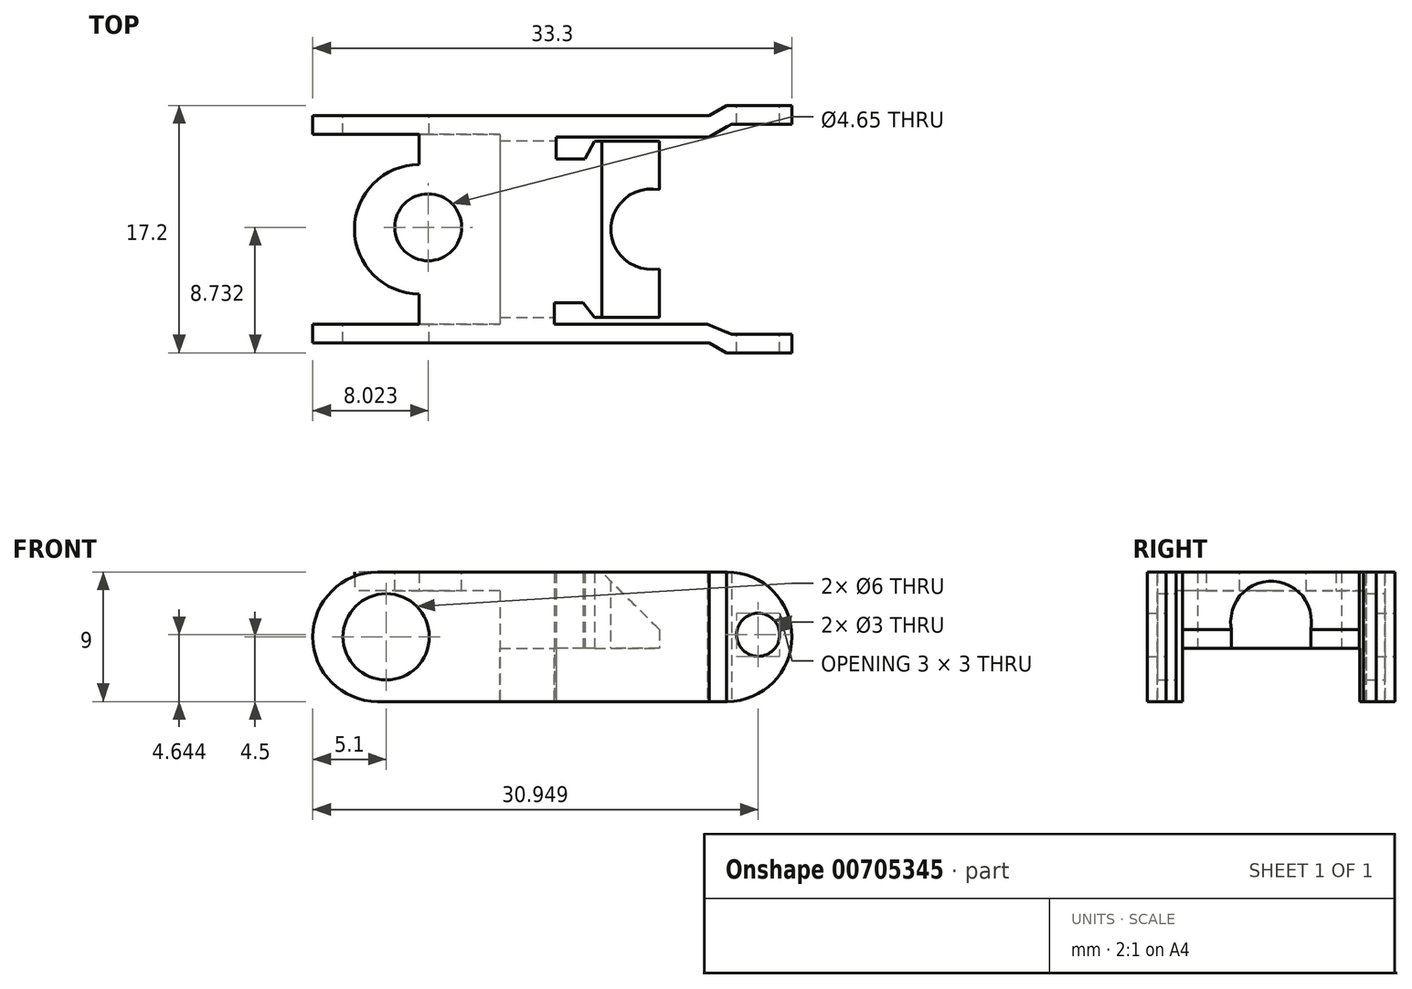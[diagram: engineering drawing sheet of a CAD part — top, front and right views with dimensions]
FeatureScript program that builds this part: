
annotation { "Feature Type Name" : "Feature", "Feature Type Description" : "" }
export const myFeature = defineFeature(function(context is Context, id is Id, definition is map)
    precondition{}
    {
        {
            var Q0;
            Q0=qCreatedBy(makeId("Top.planeOp"),FACE);
            var sketch = newSketch(context, id + "F0", { "sketchPlane" : qUnion([Q0])});
            skLineSegment(sketch, "E0", {"start": v(0, 0) * mm, "end": v(0, 1.3) * mm});
            skLineSegment(sketch, "E1", {"start": v(0, 1.3) * mm, "end": v(7.4, 1.3) * mm});
            skLineSegment(sketch, "E2", {"start": v(7.4, 1.3) * mm, "end": v(7.4, 3.4) * mm});
            skArc(sketch, "E3", {"start": v(7.4, 12.4) * mm, "mid": v(2.9, 7.9) * mm, "end": v(7.4, 3.4) * mm});
            skLineSegment(sketch, "E4", {"start": v(0, 0) * mm, "end": v(27.53, 0) * mm});
            skLineSegment(sketch, "E5", {"start": v(16.8, 1.3) * mm, "end": v(16.8, 2.8) * mm});
            skLineSegment(sketch, "E6", {"start": v(16.8, 2.8) * mm, "end": v(18.8, 2.8) * mm});
            skLineSegment(sketch, "E7", {"start": v(18.8, 2.8) * mm, "end": v(19.58, 1.76) * mm});
            skLineSegment(sketch, "E8", {"start": v(19.58, 1.76) * mm, "end": v(24.08, 1.76) * mm});
            skLineSegment(sketch, "E9", {"start": v(24.08, 1.76) * mm, "end": v(24.08, 5.15) * mm});
            skLineSegment(sketch, "E10", {"start": v(27.43, 1.3) * mm, "end": v(16.8, 1.3) * mm});
            skLineSegment(sketch, "E11.MirrorCS", {"start": v(7.4, 14.5) * mm, "end": v(7.4, 12.4) * mm});
            skLineSegment(sketch, "E12.MirrorCS", {"start": v(0, 14.5) * mm, "end": v(7.4, 14.5) * mm});
            skLineSegment(sketch, "E13.MirrorCS", {"start": v(0, 15.8) * mm, "end": v(0, 14.5) * mm});
            skLineSegment(sketch, "E14.MirrorCS", {"start": v(0, 15.8) * mm, "end": v(27.53, 15.8) * mm});
            skLineSegment(sketch, "E15.MirrorCS", {"start": v(16.9, 12.8) * mm, "end": v(18.9, 12.8) * mm});
            skLineSegment(sketch, "E16.MirrorCS", {"start": v(16.9, 14.3) * mm, "end": v(16.9, 12.8) * mm});
            skLineSegment(sketch, "E17.MirrorCS", {"start": v(27.53, 14.3) * mm, "end": v(16.9, 14.3) * mm});
            skLineSegment(sketch, "E18.MirrorCS", {"start": v(24.08, 14.04) * mm, "end": v(24.08, 10.65) * mm});
            skPoint(sketch, "E19.end.orphan", {"position": v(27.53, 0) * mm});
            skPoint(sketch, "E20.trimOffspring.end.orphan", {"position": v(37.89, 7.9) * mm});
            skLineSegment(sketch, "E21", {"start": v(7.4, 7.9) * mm, "end": v(37.89, 7.9) * mm, "construction": true});
            skLineSegment(sketch, "E22", {"start": v(7.4, 3.4) * mm, "end": v(7.4, 12.4) * mm, "construction": true});
            skPoint(sketch, "E23.orphan", {"position": v(0, 15.8) * mm});
            skLineSegment(sketch, "E24", {"start": v(27.53, 15.8) * mm, "end": v(27.53, 13.9) * mm, "construction": true});
            skLineSegment(sketch, "E25", {"start": v(27.53, 15.8) * mm, "end": v(28.75, 16.5) * mm});
            skLineSegment(sketch, "E26", {"start": v(28.75, 16.5) * mm, "end": v(33.3, 16.5) * mm});
            skLineSegment(sketch, "E27", {"start": v(33.3, 16.5) * mm, "end": v(33.3, 15.2) * mm});
            skLineSegment(sketch, "E28", {"start": v(33.3, 15.2) * mm, "end": v(29.1, 15.2) * mm});
            skLineSegment(sketch, "E29", {"start": v(29.1, 15.2) * mm, "end": v(27.53, 14.3) * mm});
            skLineSegment(sketch, "E30.MirrorCS", {"start": v(28.75, -0.7) * mm, "end": v(33.3, -0.7) * mm});
            skLineSegment(sketch, "E31.MirrorCS", {"start": v(33.3, 0.6) * mm, "end": v(29.1, 0.6) * mm});
            skLineSegment(sketch, "E32.MirrorCS", {"start": v(33.3, -0.7) * mm, "end": v(33.3, 0.6) * mm});
            skLineSegment(sketch, "E33.MirrorCS", {"start": v(27.53, 0) * mm, "end": v(28.75, -0.7) * mm});
            skLineSegment(sketch, "E34", {"start": v(27.43, 1.3) * mm, "end": v(29.1, 0.6) * mm});
            skLineSegment(sketch, "E35.MirrorCS", {"start": v(19.58, 14.04) * mm, "end": v(24.08, 14.04) * mm});
            skLineSegment(sketch, "E36", {"start": v(18.9, 12.8) * mm, "end": v(19.58, 14.04) * mm});
            skArc(sketch, "E37", {"start": v(24.08, 10.65) * mm, "mid": v(20.7, 7.9) * mm, "end": v(24.08, 5.15) * mm});
            skSolve(sketch);
        }
        {
            var Q0;
            Q0 = qSketchRegion(id + "F0", true);
            extrude(context, id + "F1", {"entities" : qUnion([Q0]), "depth" : 9 * mm, "offsetDistance" : 25 * mm});
        }
        {
            var Q0;
            Q0=makeQuery(id+"F1.opExtrude","SWEPT_FACE",FACE,{"disambiguationData":[OSD([sQuery(id+"F0.wireOp",EDGE,"E0")])]});
            var sketch = newSketch(context, id + "F2", { "sketchPlane" : qUnion([Q0])});
            skLineSegment(sketch, "E38.bottom", {"start": v(-14.5, 7.7) * mm, "end": v(-1.3, 7.7) * mm});
            skLineSegment(sketch, "E38.top", {"start": v(-14.5, 0) * mm, "end": v(-1.3, 0) * mm});
            skLineSegment(sketch, "E38.left", {"start": v(-14.5, 7.7) * mm, "end": v(-14.5, 0) * mm});
            skLineSegment(sketch, "E38.right", {"start": v(-1.3, 7.7) * mm, "end": v(-1.3, 0) * mm});
            skSolve(sketch);
        }
        {
            var Q0;
            Q0 = qSketchRegion(id + "F2", true);
            extrude(context, id + "F3", {"entities" : qUnion([Q0]), "operationType" : NewBodyOperationType.REMOVE, "oppositeDirection" : true, "depth" : 13 * mm, "offsetDistance" : 25 * mm});
        }
        {
            var Q0;
            Q0=makeQuery(id+"F1.opExtrude","CAP_EDGE",EDGE,{"disambiguationData":[OSD([sQuery(id+"F0.wireOp",EDGE,"E9")])],"isStart":false});
            var Q1;
            Q1=makeQuery(id+"F1.opExtrude","CAP_EDGE",EDGE,{"disambiguationData":[OSD([sQuery(id+"F0.wireOp",EDGE,"E18.MirrorCS")])],"isStart":false});
            chamfer(context, id + "F4", {"entities" : qUnion([Q0, Q1]), "width" : 4 * mm, "tangentPropagation" : true});
        }
        {
            var Q0;
            Q0=makeQuery(id+"F1.opExtrude","CAP_EDGE",EDGE,{"disambiguationData":[OSD([sQuery(id+"F0.wireOp",EDGE,"E32.MirrorCS")])],"isStart":true});
            var Q1;
            Q1=makeQuery(id+"F1.opExtrude","CAP_EDGE",EDGE,{"disambiguationData":[OSD([sQuery(id+"F0.wireOp",EDGE,"E32.MirrorCS")])],"isStart":false});
            var Q2;
            Q2=makeQuery(id+"F1.opExtrude","CAP_EDGE",EDGE,{"disambiguationData":[OSD([sQuery(id+"F0.wireOp",EDGE,"E27")])],"isStart":true});
            var Q3;
            Q3=makeQuery(id+"F1.opExtrude","CAP_EDGE",EDGE,{"disambiguationData":[OSD([sQuery(id+"F0.wireOp",EDGE,"E27")])],"isStart":false});
            var Q4;
            Q4=makeQuery(id+"F1.opExtrude","CAP_EDGE",EDGE,{"disambiguationData":[OSD([sQuery(id+"F0.wireOp",EDGE,"E13.MirrorCS")])],"isStart":true});
            var Q5;
            Q5=makeQuery(id+"F1.opExtrude","CAP_EDGE",EDGE,{"disambiguationData":[OSD([sQuery(id+"F0.wireOp",EDGE,"E13.MirrorCS")])],"isStart":false});
            var Q6;
            Q6=makeQuery(id+"F1.opExtrude","CAP_EDGE",EDGE,{"disambiguationData":[OSD([sQuery(id+"F0.wireOp",EDGE,"E0")])],"isStart":true});
            var Q7;
            Q7=makeQuery(id+"F1.opExtrude","CAP_EDGE",EDGE,{"disambiguationData":[OSD([sQuery(id+"F0.wireOp",EDGE,"E0")])],"isStart":false});
            fillet(context, id + "F5", {"entities" : qUnion([Q0, Q1, Q2, Q3, Q4, Q5, Q6, Q7]), "radius" : 4.5 * mm, "tangentPropagation" : true, "allowEdgeOverflow" : false});
        }
        {
            var Q0;
            Q0=makeQuery(id+"F1.opExtrude","SWEPT_FACE",FACE,{"disambiguationData":[OSD([sQuery(id+"F0.wireOp",EDGE,"E14.MirrorCS")])]});
            var sketch = newSketch(context, id + "F6", { "sketchPlane" : qUnion([Q0])});
            skCircle(sketch, "E39", {"center": v(-5.1, 4.5) * mm, "radius": 3 * mm});
            skSolve(sketch);
        }
        {
            var Q0;
            Q0=makeQuery(id+"F1.opExtrude","CAP_FACE",FACE,{"disambiguationData":[OSD([sQuery(id+"F0.wireOp",EDGE,"E0"),sQuery(id+"F0.wireOp",EDGE,"E1"),sQuery(id+"F0.wireOp",EDGE,"E2"),sQuery(id+"F0.wireOp",EDGE,"E3"),sQuery(id+"F0.wireOp",EDGE,"E4"),sQuery(id+"F0.wireOp",EDGE,"E5"),sQuery(id+"F0.wireOp",EDGE,"E6"),sQuery(id+"F0.wireOp",EDGE,"E7"),sQuery(id+"F0.wireOp",EDGE,"E8"),sQuery(id+"F0.wireOp",EDGE,"E9"),sQuery(id+"F0.wireOp",EDGE,"E10"),sQuery(id+"F0.wireOp",EDGE,"E11.MirrorCS"),sQuery(id+"F0.wireOp",EDGE,"E12.MirrorCS"),sQuery(id+"F0.wireOp",EDGE,"E13.MirrorCS"),sQuery(id+"F0.wireOp",EDGE,"E15.MirrorCS"),sQuery(id+"F0.wireOp",EDGE,"E16.MirrorCS"),sQuery(id+"F0.wireOp",EDGE,"E17.MirrorCS"),sQuery(id+"F0.wireOp",EDGE,"13fdda64-d4ae-4b14-ad6a-07e018b78b787.MirrorCS"),sQuery(id+"F0.wireOp",EDGE,"13fdda64-d4ae-4b14-ad6a-07e018b78b788.MirrorCS"),sQuery(id+"F0.wireOp",EDGE,"E14.MirrorCS"),sQuery(id+"F0.wireOp",EDGE,"E18.MirrorCS"),sQuery(id+"F0.wireOp",EDGE,"QRLhJHuq-ugKA-eGBM-L1QN-SyeUm9ubxrph"),sQuery(id+"F0.wireOp",EDGE,"E25"),sQuery(id+"F0.wireOp",EDGE,"E26"),sQuery(id+"F0.wireOp",EDGE,"E27"),sQuery(id+"F0.wireOp",EDGE,"E28"),sQuery(id+"F0.wireOp",EDGE,"E29"),sQuery(id+"F0.wireOp",EDGE,"E30.MirrorCS"),sQuery(id+"F0.wireOp",EDGE,"E31.MirrorCS"),sQuery(id+"F0.wireOp",EDGE,"E32.MirrorCS"),sQuery(id+"F0.wireOp",EDGE,"E33.MirrorCS"),sQuery(id+"F0.wireOp",EDGE,"E34")])],"isStart":false});
            var sketch = newSketch(context, id + "F7", { "sketchPlane" : qUnion([Q0])});
            skCircle(sketch, "E40", {"center": v(8.02, 8.03) * mm, "radius": 2.33 * mm});
            skSolve(sketch);
        }
        {
            var Q0;
            Q0 = qSketchRegion(id + "F7", true);
            extrude(context, id + "F8", {"entities" : qUnion([Q0]), "operationType" : NewBodyOperationType.REMOVE, "endBound" : BoundingType.THROUGH_ALL, "oppositeDirection" : true, "depth" : 25 * mm, "offsetDistance" : 25 * mm});
        }
        {
            var Q0;
            Q0=makeQuery(id+"F4.opChamfer","BLEND_FACE",FACE,{"disambiguationData":[OSD([sQuery(id+"F0.wireOp",EDGE,"E9")])]});
            cPlane(context, id + "F9", {"entities" : qUnion([Q0]), "cplaneType" : CPlaneType.OFFSET, "offset" : 1.3 * mm, "oppositeDirection" : true, "width" : 150 * mm, "height" : 150 * mm});
        }
        {
            var Q0;
            Q0 = qSketchRegion(id + "F6", true);
            extrude(context, id + "F10", {"entities" : qUnion([Q0]), "operationType" : NewBodyOperationType.REMOVE, "endBound" : BoundingType.THROUGH_ALL, "oppositeDirection" : true, "depth" : 25 * mm, "offsetDistance" : 25 * mm});
        }
        {
            var Q0;
            Q0=makeQuery(id+"F1.opExtrude","SWEPT_FACE",FACE,{"disambiguationData":[OSD([sQuery(id+"F0.wireOp",EDGE,"E9")])]});
            var sketch = newSketch(context, id + "F11", { "sketchPlane" : qUnion([Q0])});
            skLineSegment(sketch, "E41.bottom", {"start": v(1.76, 3.7) * mm, "end": v(14.05, 3.7) * mm});
            skLineSegment(sketch, "E41.top", {"start": v(1.76, 0) * mm, "end": v(14.05, 0) * mm});
            skLineSegment(sketch, "E41.left", {"start": v(1.76, 3.7) * mm, "end": v(1.76, 0) * mm});
            skLineSegment(sketch, "E41.right", {"start": v(14.05, 3.7) * mm, "end": v(14.05, 0) * mm});
            skSolve(sketch);
        }
        {
            var Q0;
            Q0 = qSketchRegion(id + "F11", true);
            extrude(context, id + "F12", {"entities" : qUnion([Q0]), "operationType" : NewBodyOperationType.REMOVE, "endBound" : BoundingType.THROUGH_ALL, "oppositeDirection" : true, "depth" : 25 * mm, "offsetDistance" : 25 * mm});
        }
        {
            var Q0;
            Q0=makeQuery(id+"F1.opExtrude","SWEPT_FACE",FACE,{"disambiguationData":[OSD([sQuery(id+"F0.wireOp",EDGE,"E26")])]});
            var sketch = newSketch(context, id + "F13", { "sketchPlane" : qUnion([Q0])});
            skCircle(sketch, "E42", {"center": v(-30.95, 4.64) * mm, "radius": 1.5 * mm});
            skSolve(sketch);
        }
        {
            var Q0;
            Q0 = qSketchRegion(id + "F13", true);
            extrude(context, id + "F14", {"entities" : qUnion([Q0]), "operationType" : NewBodyOperationType.REMOVE, "endBound" : BoundingType.THROUGH_ALL, "oppositeDirection" : true, "depth" : 25 * mm, "offsetDistance" : 25 * mm});
        }
    });
